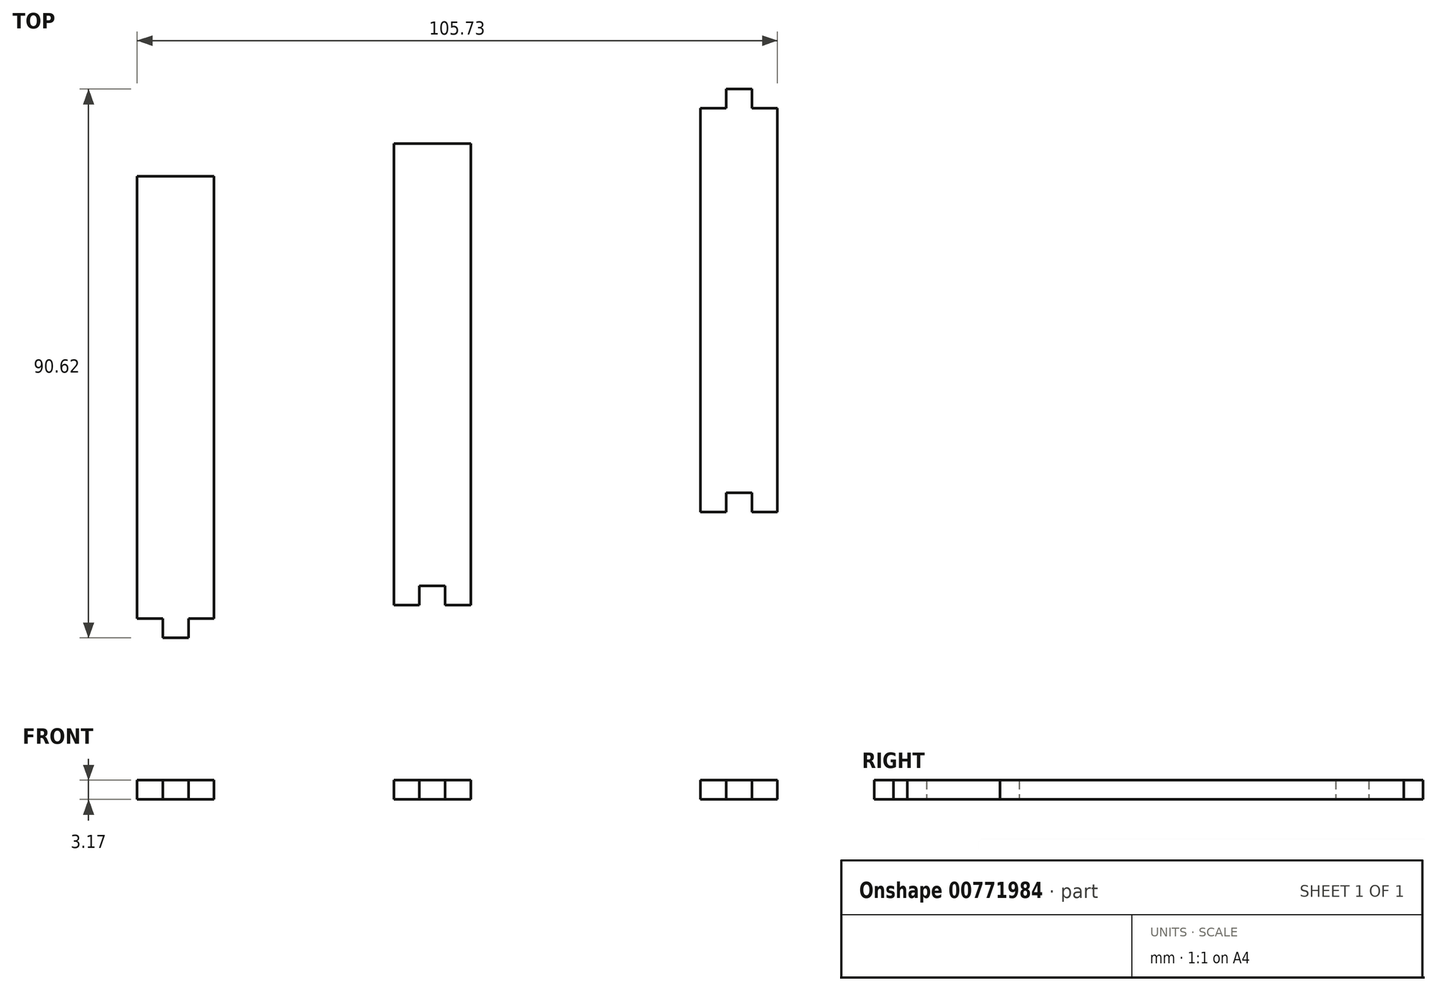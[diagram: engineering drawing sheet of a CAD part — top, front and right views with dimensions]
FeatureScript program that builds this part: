
annotation { "Feature Type Name" : "Feature", "Feature Type Description" : "" }
export const myFeature = defineFeature(function(context is Context, id is Id, definition is map)
    precondition{}
    {
        {
            var Q0;
            Q0=qCreatedBy(makeId("Top.planeOp"),FACE);
            var sketch = newSketch(context, id + "F0", { "sketchPlane" : qUnion([Q0])});
            skLineSegment(sketch, "E0", {"start": v(-112.27, 29.37) * mm, "end": v(-99.57, 29.37) * mm});
            skLineSegment(sketch, "E1", {"start": v(-99.57, 29.37) * mm, "end": v(-99.57, -43.66) * mm});
            skLineSegment(sketch, "E2", {"start": v(-99.57, -43.66) * mm, "end": v(-112.27, -43.66) * mm});
            skLineSegment(sketch, "E3", {"start": v(-112.27, -43.66) * mm, "end": v(-112.27, 29.37) * mm});
            skLineSegment(sketch, "E4", {"start": v(-69.88, 34.8) * mm, "end": v(-57.18, 34.8) * mm});
            skLineSegment(sketch, "E5", {"start": v(-57.18, 34.8) * mm, "end": v(-57.18, -41.4) * mm});
            skLineSegment(sketch, "E6", {"start": v(-57.18, -41.4) * mm, "end": v(-69.88, -41.4) * mm});
            skLineSegment(sketch, "E7", {"start": v(-69.88, -41.4) * mm, "end": v(-69.88, 34.8) * mm});
            skLineSegment(sketch, "E8", {"start": v(-19.24, 40.61) * mm, "end": v(-6.54, 40.61) * mm});
            skLineSegment(sketch, "E9", {"start": v(-6.54, 40.61) * mm, "end": v(-6.54, -22.89) * mm});
            skLineSegment(sketch, "E10", {"start": v(-6.54, -22.89) * mm, "end": v(-19.24, -22.89) * mm});
            skLineSegment(sketch, "E11", {"start": v(-19.24, -22.89) * mm, "end": v(-19.24, 40.61) * mm});
            skSolve(sketch);
        }
        {
            var Q0;
            Q0 = qSketchRegion(id + "F0", true);
            extrude(context, id + "F1", {"entities" : qUnion([Q0]), "depth" : 3.17 * mm, "offsetDistance" : 25.4 * mm});
        }
        {
            var Q0;
            Q0=makeQuery(id+"F1.opExtrude","SWEPT_FACE",FACE,{"disambiguationData":[OSD([sQuery(id+"F0.wireOp",EDGE,"E0")])]});
            var sketch = newSketch(context, id + "F2", { "sketchPlane" : qUnion([Q0])});
            skLineSegment(sketch, "E12.bottom", {"start": v(10.77, 3.18) * mm, "end": v(15, 3.18) * mm});
            skLineSegment(sketch, "E12.top", {"start": v(10.77, 0) * mm, "end": v(15, 0) * mm});
            skLineSegment(sketch, "E12.left", {"start": v(10.77, 3.18) * mm, "end": v(10.77, 0) * mm});
            skLineSegment(sketch, "E12.right", {"start": v(15, 3.18) * mm, "end": v(15, 0) * mm});
            skSolve(sketch);
        }
        {
            var Q0;
            Q0 = qSketchRegion(id + "F2", true);
            extrude(context, id + "F3", {"entities" : qUnion([Q0]), "operationType" : NewBodyOperationType.ADD, "depth" : 11.1 * mm, "offsetDistance" : 25.4 * mm});
        }
        {
            var Q0;
            Q0=makeQuery(id+"F1.opExtrude","SWEPT_FACE",FACE,{"disambiguationData":[OSD([sQuery(id+"F0.wireOp",EDGE,"E10")])]});
            var sketch = newSketch(context, id + "F4", { "sketchPlane" : qUnion([Q0])});
            skLineSegment(sketch, "E13.bottom", {"start": v(-15, 3.18) * mm, "end": v(-10.77, 3.18) * mm});
            skLineSegment(sketch, "E13.top", {"start": v(-15, 0) * mm, "end": v(-10.77, 0) * mm});
            skLineSegment(sketch, "E13.left", {"start": v(-15, 3.18) * mm, "end": v(-15, 0) * mm});
            skLineSegment(sketch, "E13.right", {"start": v(-10.77, 3.18) * mm, "end": v(-10.77, 0) * mm});
            skSolve(sketch);
        }
        {
            var Q0;
            {var subQ0=sQuery(id+"F4.wireOp",EDGE,"E13.left");Q0=makeQuery(id+"F4.imprint","IMPRINT",FACE,{"disambiguationData":[TD([[makeQuery(id+"F4.imprint","IMPRINT",EDGE,{"derivedFrom":subQ0}),-1.0]])]});}
            var Q1;
            {var subQ0=sQuery(id+"F4.wireOp",EDGE,"E13.right");Q1=makeQuery(id+"F4.imprint","IMPRINT",FACE,{"disambiguationData":[TD([[makeQuery(id+"F4.imprint","IMPRINT",EDGE,{"derivedFrom":subQ0}),1.0]])]});}
            extrude(context, id + "F5", {"entities" : qUnion([Q0, Q1]), "operationType" : NewBodyOperationType.ADD, "depth" : 3.17 * mm, "offsetDistance" : 25.4 * mm});
        }
        {
            var Q0;
            Q0=makeQuery(id+"F1.opExtrude","SWEPT_FACE",FACE,{"disambiguationData":[OSD([sQuery(id+"F0.wireOp",EDGE,"E2")])]});
            var sketch = newSketch(context, id + "F6", { "sketchPlane" : qUnion([Q0])});
            skLineSegment(sketch, "E14.bottom", {"start": v(-108.04, 3.18) * mm, "end": v(-103.8, 3.18) * mm});
            skLineSegment(sketch, "E14.top", {"start": v(-108.04, 0) * mm, "end": v(-103.8, 0) * mm});
            skLineSegment(sketch, "E14.left", {"start": v(-108.04, 3.18) * mm, "end": v(-108.04, 0) * mm});
            skLineSegment(sketch, "E14.right", {"start": v(-103.8, 3.18) * mm, "end": v(-103.8, 0) * mm});
            skSolve(sketch);
        }
        {
            var Q0;
            Q0 = qSketchRegion(id + "F6", true);
            extrude(context, id + "F7", {"entities" : qUnion([Q0]), "operationType" : NewBodyOperationType.ADD, "depth" : 3.17 * mm, "offsetDistance" : 25.4 * mm});
        }
        {
            var Q0;
            Q0=makeQuery(id+"F1.opExtrude","SWEPT_FACE",FACE,{"disambiguationData":[OSD([sQuery(id+"F0.wireOp",EDGE,"E6")])]});
            var sketch = newSketch(context, id + "F8", { "sketchPlane" : qUnion([Q0])});
            skLineSegment(sketch, "E15.bottom", {"start": v(-65.65, 3.18) * mm, "end": v(-61.42, 3.18) * mm});
            skLineSegment(sketch, "E15.top", {"start": v(-65.65, 0) * mm, "end": v(-61.42, 0) * mm});
            skLineSegment(sketch, "E15.left", {"start": v(-65.65, 3.18) * mm, "end": v(-65.65, 0) * mm});
            skLineSegment(sketch, "E15.right", {"start": v(-61.42, 3.18) * mm, "end": v(-61.42, 0) * mm});
            skSolve(sketch);
        }
        {
            var Q0;
            Q0=makeQuery(id+"F8.imprint","IMPRINT",FACE,{"disambiguationData":[TD([[makeQuery(id+"F8.imprint","IMPRINT",EDGE,{"derivedFrom":sQuery(id+"F8.wireOp",EDGE,"E15.bottom")}),1.0]])]});
            extrude(context, id + "F9", {"entities" : qUnion([Q0]), "operationType" : NewBodyOperationType.REMOVE, "oppositeDirection" : true, "depth" : 3.17 * mm, "offsetDistance" : 25.4 * mm});
        }
        {
            var Q0;
            Q0=makeQuery(id+"F1.opExtrude","SWEPT_FACE",FACE,{"disambiguationData":[OSD([sQuery(id+"F0.wireOp",EDGE,"E8")])]});
            var sketch = newSketch(context, id + "F10", { "sketchPlane" : qUnion([Q0])});
            skLineSegment(sketch, "E16.bottom", {"start": v(10.77, 3.18) * mm, "end": v(15, 3.18) * mm});
            skLineSegment(sketch, "E16.top", {"start": v(10.77, 0) * mm, "end": v(15, 0) * mm});
            skLineSegment(sketch, "E16.left", {"start": v(10.77, 3.18) * mm, "end": v(10.77, 0) * mm});
            skLineSegment(sketch, "E16.right", {"start": v(15, 3.18) * mm, "end": v(15, 0) * mm});
            skSolve(sketch);
        }
        {
            var Q0;
            Q0=makeQuery(id+"F10.imprint","IMPRINT",FACE,{"disambiguationData":[TD([[makeQuery(id+"F10.imprint","IMPRINT",EDGE,{"derivedFrom":sQuery(id+"F10.wireOp",EDGE,"E16.bottom")}),1.0]])]});
            extrude(context, id + "F11", {"entities" : qUnion([Q0]), "operationType" : NewBodyOperationType.ADD, "depth" : 3.17 * mm, "offsetDistance" : 25.4 * mm});
        }
    });
